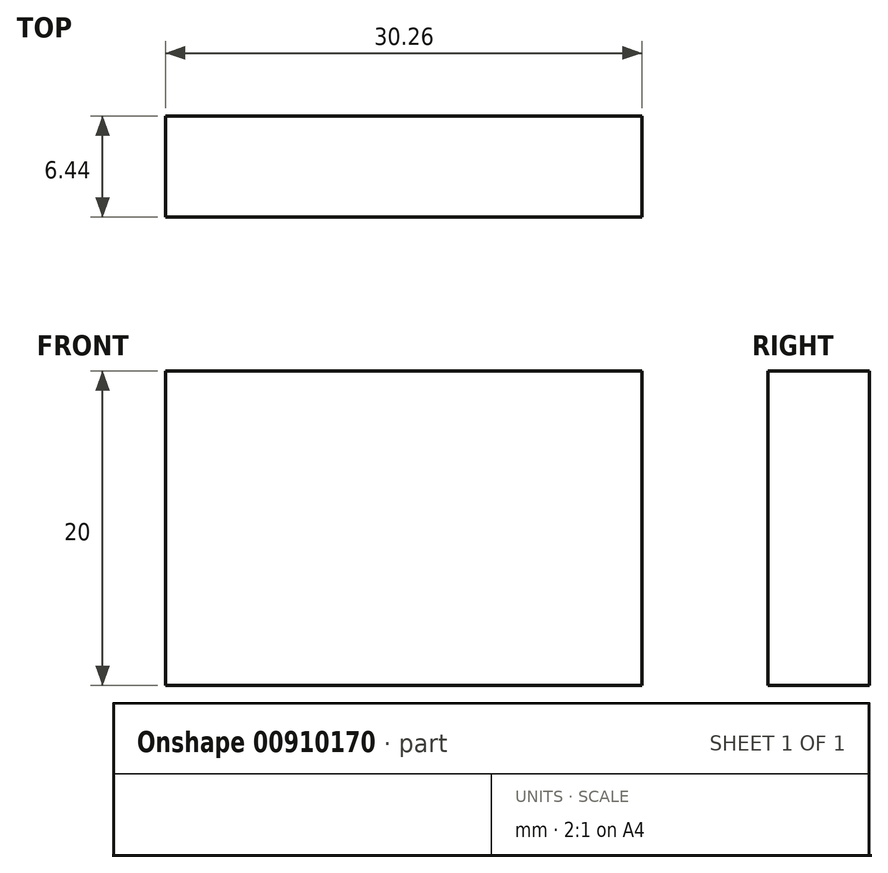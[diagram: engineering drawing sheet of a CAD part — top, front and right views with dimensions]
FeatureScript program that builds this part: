
annotation { "Feature Type Name" : "Feature", "Feature Type Description" : "" }
export const myFeature = defineFeature(function(context is Context, id is Id, definition is map)
    precondition{}
    {
        {
            var Q0;
            Q0=qCreatedBy(makeId("Top.planeOp"),FACE);
            var sketch = newSketch(context, id + "F0", { "sketchPlane" : qUnion([Q0])});
            skLineSegment(sketch, "E0.bottom", {"start": v(15.13, -3.22) * mm, "end": v(-15.13, -3.22) * mm});
            skLineSegment(sketch, "E0.top", {"start": v(15.13, 3.22) * mm, "end": v(-15.13, 3.22) * mm});
            skLineSegment(sketch, "E0.left", {"start": v(15.13, -3.22) * mm, "end": v(15.13, 3.22) * mm});
            skLineSegment(sketch, "E0.right", {"start": v(-15.13, -3.22) * mm, "end": v(-15.13, 3.22) * mm});
            skPoint(sketch, "E0.middle", {"position": v(0, 0) * mm});
            skSolve(sketch);
        }
        {
            var Q0;
            Q0=makeQuery(id+"F0.imprint","IMPRINT",FACE,{"disambiguationData":[TD([[makeQuery(id+"F0.imprint","IMPRINT",EDGE,{"derivedFrom":sQuery(id+"F0.wireOp",EDGE,"E0.bottom")}),-1.0]])]});
            extrude(context, id + "F1", {"entities" : qUnion([Q0]), "depth" : 20 * mm, "offsetDistance" : 25 * mm});
        }
    });
